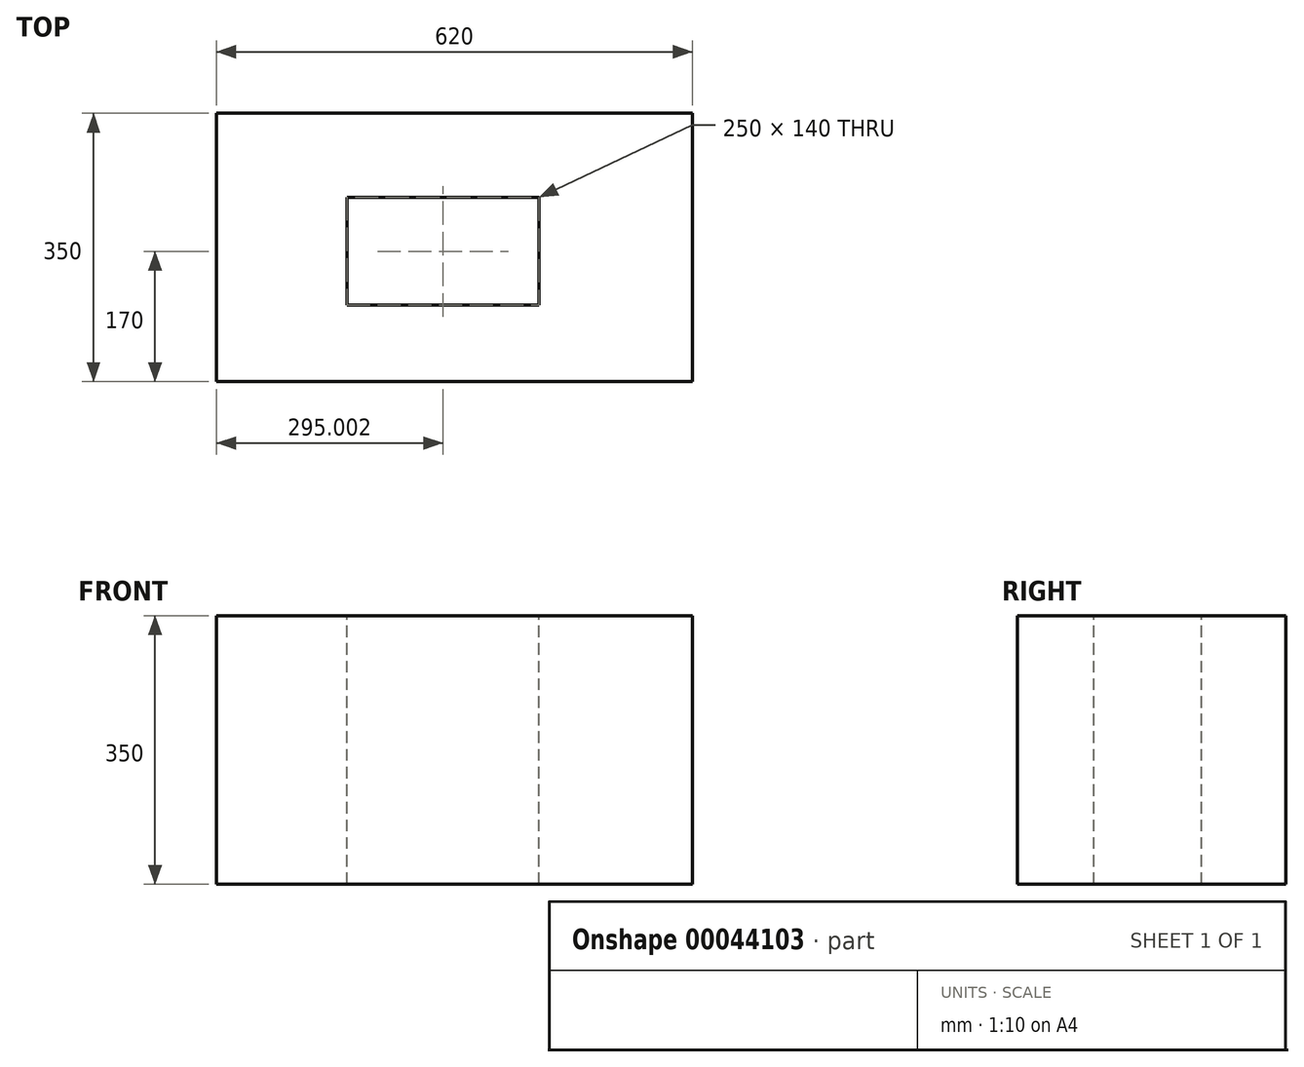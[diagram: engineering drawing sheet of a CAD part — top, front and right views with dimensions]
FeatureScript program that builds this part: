
annotation { "Feature Type Name" : "Feature", "Feature Type Description" : "" }
export const myFeature = defineFeature(function(context is Context, id is Id, definition is map)
    precondition{}
    {
        {
            var Q0;
            Q0=qCreatedBy(makeId("Front.planeOp"),FACE);
            var sketch = newSketch(context, id + "F3", { "sketchPlane" : qUnion([Q0])});
            skLineSegment(sketch, "E0.rect.bottom", {"start": v(123.91, 175) * mm, "end": v(-496.09, 175) * mm});
            skLineSegment(sketch, "E0.rect.top", {"start": v(123.91, -175) * mm, "end": v(-496.09, -175) * mm});
            skLineSegment(sketch, "E0.rect.left", {"start": v(123.91, 175) * mm, "end": v(123.91, -175) * mm});
            skLineSegment(sketch, "E0.rect.right", {"start": v(-496.09, 175) * mm, "end": v(-496.09, -175) * mm});
            skPoint(sketch, "E0.rect.middle", {"position": v(-186.09, 0) * mm});
            skSolve(sketch);
        }
        {
            var Q0;
            Q0 = qSketchRegion(id + "F3", true);
            var Q1;
            Q1=sQuery(id+"F3.wireOp",EDGE,"E0.rect.top");
            var Q2;
            Q2=sQuery(id+"F3.wireOp",EDGE,"E0.rect.left");
            var Q3;
            Q3=sQuery(id+"F3.wireOp",EDGE,"E0.rect.bottom");
            var Q4;
            Q4=sQuery(id+"F3.wireOp",EDGE,"E0.rect.right");
            extrude(context, id + "F0", {"entities" : qUnion([Q0]), "surfaceEntities" : qUnion([Q1, Q2, Q3, Q4]), "depth" : 350 * mm});
        }
        {
            var Q0;
            Q0=makeQuery(id+"F0.opExtrude","SWEPT_FACE",FACE,{"disambiguationData":[OSD([sQuery(id+"F3.wireOp",EDGE,"E0.rect.bottom")])]});
            var sketch = newSketch(context, id + "F1", { "sketchPlane" : qUnion([Q0])});
            skLineSegment(sketch, "E1", {"start": v(-326.09, -110) * mm, "end": v(-76.09, -110) * mm});
            skLineSegment(sketch, "E2", {"start": v(-76.09, -110) * mm, "end": v(-76.09, -250) * mm});
            skLineSegment(sketch, "E3", {"start": v(-76.09, -250) * mm, "end": v(-326.09, -250) * mm});
            skLineSegment(sketch, "E4", {"start": v(-326.09, -250) * mm, "end": v(-326.09, -110) * mm});
            skSolve(sketch);
        }
        {
            var Q0;
            Q0 = qSketchRegion(id + "F1", true);
            extrude(context, id + "F2", {"entities" : qUnion([Q0]), "operationType" : NewBodyOperationType.REMOVE, "endBound" : BoundingType.THROUGH_ALL, "oppositeDirection" : true, "depth" : 25 * mm});
        }
    });
